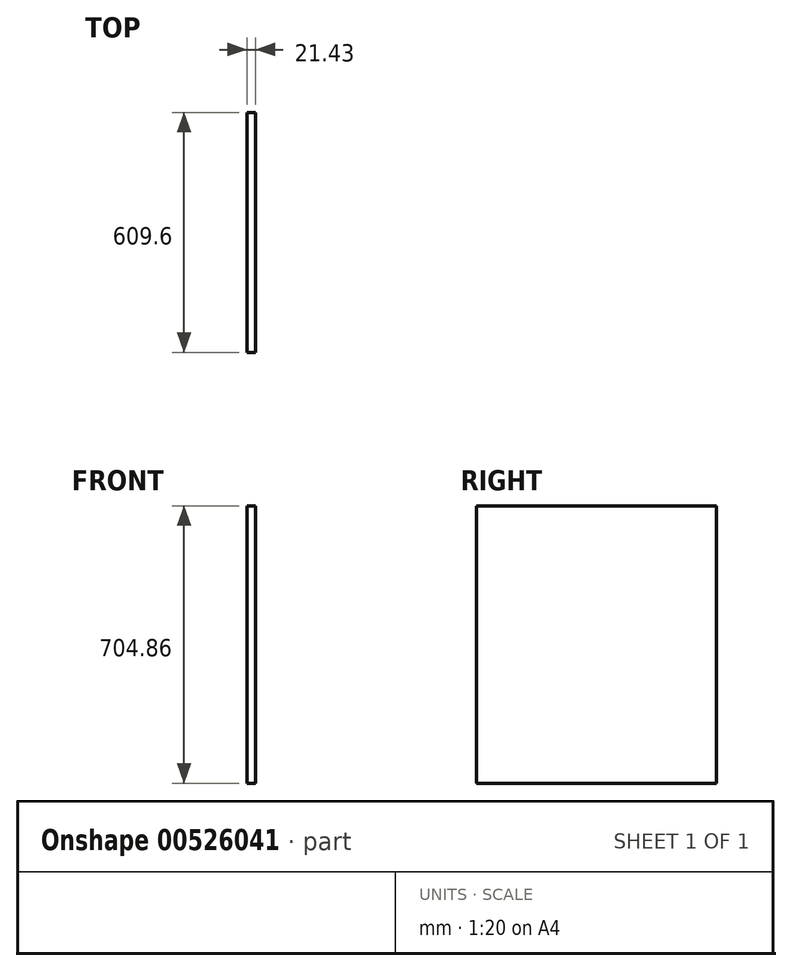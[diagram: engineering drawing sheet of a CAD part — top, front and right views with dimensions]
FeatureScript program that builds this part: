
annotation { "Feature Type Name" : "Feature", "Feature Type Description" : "" }
export const myFeature = defineFeature(function(context is Context, id is Id, definition is map)
    precondition{}
    {
        {
            var Q0;
            Q0=qCreatedBy(makeId("Right.planeOp"),FACE);
            var sketch = newSketch(context, id + "F0", { "sketchPlane" : qUnion([Q0])});
            skLineSegment(sketch, "E0.bottom", {"start": v(-304.8, 352.43) * mm, "end": v(304.8, 352.43) * mm});
            skLineSegment(sketch, "E0.top", {"start": v(-304.8, -352.43) * mm, "end": v(304.8, -352.43) * mm});
            skLineSegment(sketch, "E0.left", {"start": v(-304.8, 352.43) * mm, "end": v(-304.8, -352.43) * mm});
            skLineSegment(sketch, "E0.right", {"start": v(304.8, 352.43) * mm, "end": v(304.8, -352.43) * mm});
            skLineSegment(sketch, "E1", {"start": v(0, -352.43) * mm, "end": v(0, 352.43) * mm, "construction": true});
            skSolve(sketch);
        }
        {
            var Q0;
            Q0=qSketchRegion(id+"F0",true);
            extrude(context, id + "F1", {"entities" : qUnion([Q0]), "depth" : 21.43 * mm});
        }
    });
